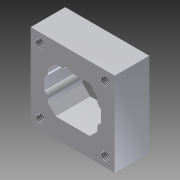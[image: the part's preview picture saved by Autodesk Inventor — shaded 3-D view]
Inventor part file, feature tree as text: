
AUTODESK INVENTOR PART (.ipt)
format: ipt  version: 2012 (Build 160160000, 160)  size: 138,752 bytes
history: native  units: in
note: dims shown in document units (in); Inventor stores cm internally (conversion verified against a paired STEP export)
features: thread x4, sketch x1, extrude x1, fillet x1, hole x1
ambient origin geometry x8: Origin, YZ Plane, XZ Plane, XY Plane, X Axis, Y Axis, Z Axis, Center Point
bodies: Solid1 (feature_tree)
feature tree (8):
  sketch  "Sketch1"  dims[d0=0.9449in d1=0.4724in d2=1.0236in d3=0.5118in d4=0.0787in d5=0.2559in d6=0.128in d7=0.0787in d8=0.5625in d9=2.0in d10=1.0in d11=2.0in d12=1.0in d13=0.1181in d14=0.3937in d15=0.1575in d16=0.1575in d17=0.1575in d18=0.1575in d19=0.1575in d20=0.2in d21=0.2in d22=0.2in d23=0.2in d24=0.719in d25=0.0in d26=0.125in d27=0.18in d28=0.75in d29=0.27in d30=0.2in d31=0.5635in d32=1.0in d33=0.8108in d34=1.6in d35=1.6in d36=1.0in d37=0.0in d38=1.0in d39=0.0in d40=1.0in d41=0.0in d42=1.0in d43=0.0in]
  extrude  "Extrusion1"  Depth=0.4724in
  fillet  "Fillet1"  Radius=1.0236in
  hole  "Hole1"  [1 undecoded]
  thread  "Thread1"  [1 undecoded]
  thread  "Thread2"  [1 undecoded]
  thread  "Thread3"  [1 undecoded]
  thread  "Thread4"  [1 undecoded]
note: 5 required parameter values undecoded (feature->parameter linkage not recoverable at this tier; creation-order binding heuristic only, values carry confidence <= 0.55)
